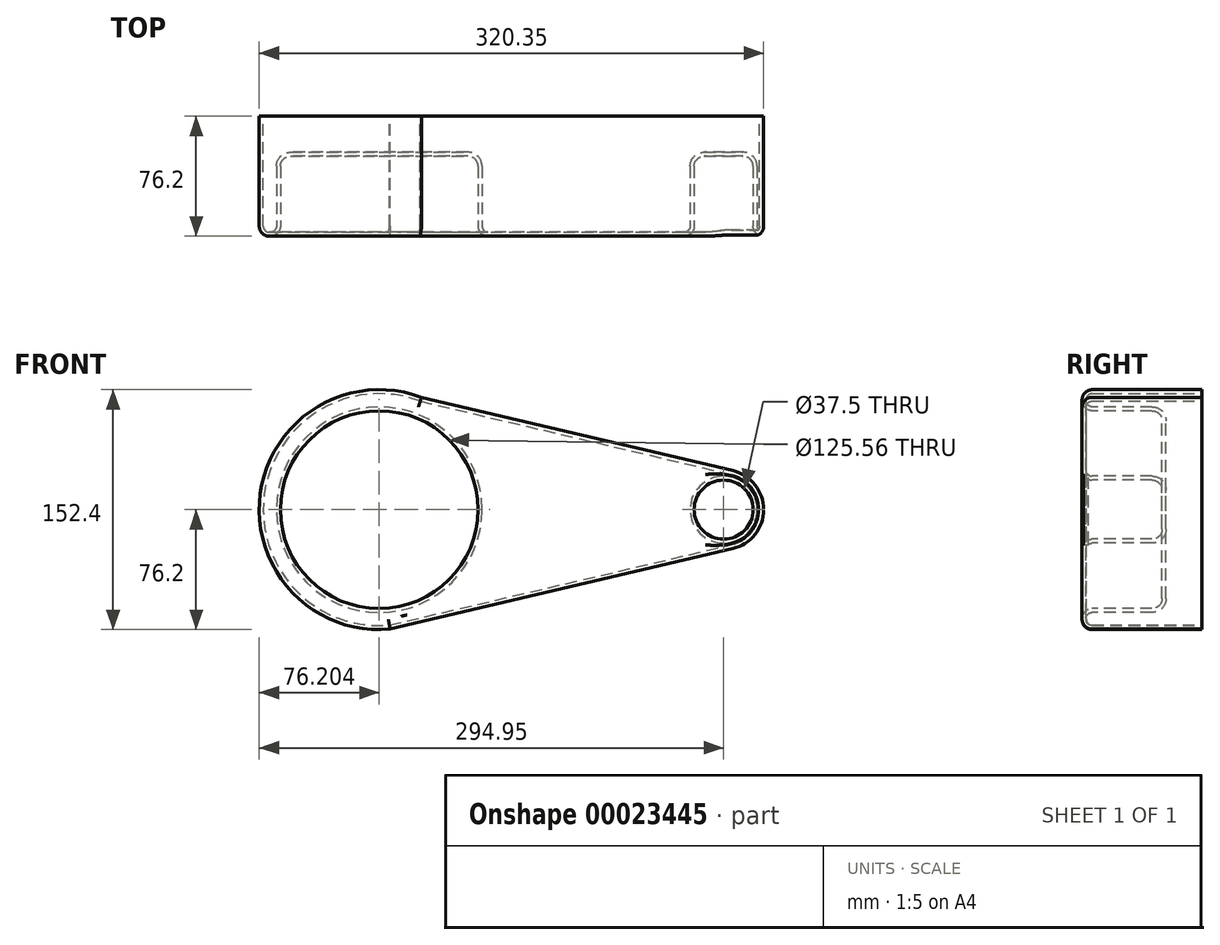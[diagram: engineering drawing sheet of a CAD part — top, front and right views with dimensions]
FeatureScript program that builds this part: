
annotation { "Feature Type Name" : "Feature", "Feature Type Description" : "" }
export const myFeature = defineFeature(function(context is Context, id is Id, definition is map)
    precondition{}
    {
        {
            var Q0;
            Q0=qCreatedBy(makeId("Front.planeOp"),FACE);
            var sketch = newSketch(context, id + "F0", { "sketchPlane" : qUnion([Q0])});
            skCircle(sketch, "E0", {"center": v(-136.36, 0) * mm, "radius": 76.2 * mm});
            skCircle(sketch, "E1", {"center": v(82.39, 0) * mm, "radius": 25.4 * mm});
            skLineSegment(sketch, "E2", {"start": v(-109.57, 71.34) * mm, "end": v(88.22, 24.72) * mm});
            skLineSegment(sketch, "E3", {"start": v(-129.5, -75.9) * mm, "end": v(88.2, -24.73) * mm});
            skSolve(sketch);
        }
        {
            var Q0;
            {var subQ5=sQuery(id+"F0.wireOp",EDGE,"E2");Q0=makeQuery(id+"F0.imprint","IMPRINT",FACE,{"disambiguationData":[TD([[makeQuery(id+"F0.imprint","IMPRINT",EDGE,{"derivedFrom":subQ5}),-1.0]])]});}
            var Q1;
            {var subQ1=sQuery(id+"F0.wireOp",EDGE,"E0");var subQ4=makeQuery(id+"F0.imprint","INTERSECT",VERTEX,{"derivedFrom":[subQ1,sQuery(id+"F0.wireOp",EDGE,"E2")]});Q1=makeQuery(id+"F0.imprint","IMPRINT",FACE,{"disambiguationData":[TD([[makeQuery(id+"F0.imprint","IMPRINT",EDGE,{"disambiguationData":[TD([[subQ4,-1.0]])],"derivedFrom":subQ1}),1.0]])]});}
            var Q2;
            {var subQ0=sQuery(id+"F0.wireOp",EDGE,"E1");var subQ2=makeQuery(id+"F0.imprint","INTERSECT",VERTEX,{"derivedFrom":[subQ0,sQuery(id+"F0.wireOp",EDGE,"E2")]});Q2=makeQuery(id+"F0.imprint","IMPRINT",FACE,{"disambiguationData":[TD([[makeQuery(id+"F0.imprint","IMPRINT",EDGE,{"disambiguationData":[TD([[subQ2,-1.0]])],"derivedFrom":subQ0}),1.0]])]});}
            extrude(context, id + "F1", {"entities" : qUnion([Q0, Q1, Q2]), "depth" : 76.2 * mm});
        }
        {
            var Q0;
            Q0=makeQuery(id+"F1.opExtrude","CAP_FACE",FACE,{"disambiguationData":[OSD([sQuery(id+"F0.wireOp",EDGE,"E0"),sQuery(id+"F0.wireOp",EDGE,"E1"),sQuery(id+"F0.wireOp",EDGE,"E2"),sQuery(id+"F0.wireOp",EDGE,"E3")])],"isStart":false});
            var sketch = newSketch(context, id + "F2", { "sketchPlane" : qUnion([Q0])});
            skCircle(sketch, "E4", {"center": v(-136.36, 0) * mm, "radius": 62.78 * mm});
            skCircle(sketch, "E5", {"center": v(82.39, 0) * mm, "radius": 18.75 * mm});
            skSolve(sketch);
        }
        {
            var Q0;
            Q0 = qSketchRegion(id + "F2", true);
            extrude(context, id + "F3", {"entities" : qUnion([Q0]), "operationType" : NewBodyOperationType.REMOVE, "oppositeDirection" : true, "depth" : 50.8 * mm});
        }
        {
            var Q0;
            Q0=makeQuery(id+"F1.opExtrude","CAP_FACE",FACE,{"disambiguationData":[OSD([sQuery(id+"F0.wireOp",EDGE,"E0"),sQuery(id+"F0.wireOp",EDGE,"E1"),sQuery(id+"F0.wireOp",EDGE,"E2"),sQuery(id+"F0.wireOp",EDGE,"E3")])],"isStart":false});
            var Q1;
            Q1=makeQuery(id+"F3.boolean.opBoolean","COPY",EDGE,{"derivedFrom":makeQuery(id+"F3.opExtrude","CAP_EDGE",EDGE,{"disambiguationData":[OSD([sQuery(id+"F2.wireOp",EDGE,"E4")])],"isStart":false})});
            var Q2;
            Q2=makeQuery(id+"F3.boolean.opBoolean","COPY",EDGE,{"derivedFrom":makeQuery(id+"F3.opExtrude","CAP_EDGE",EDGE,{"disambiguationData":[OSD([sQuery(id+"F2.wireOp",EDGE,"E5")])],"isStart":false})});
            fillet(context, id + "F4", {"entities" : qUnion([Q0, Q1, Q2]), "radius" : 6.35 * mm, "tangentPropagation" : true, "allowEdgeOverflow" : false});
        }
        {
            var Q0;
            Q0=makeQuery(id+"F1.opExtrude","CAP_FACE",FACE,{"disambiguationData":[OSD([sQuery(id+"F0.wireOp",EDGE,"E0"),sQuery(id+"F0.wireOp",EDGE,"E1"),sQuery(id+"F0.wireOp",EDGE,"E2"),sQuery(id+"F0.wireOp",EDGE,"E3")])],"isStart":true});
            shell(context, id + "F5", {"entities" : qUnion([Q0]), "thickness" : 2.54 * mm});
        }
    });
